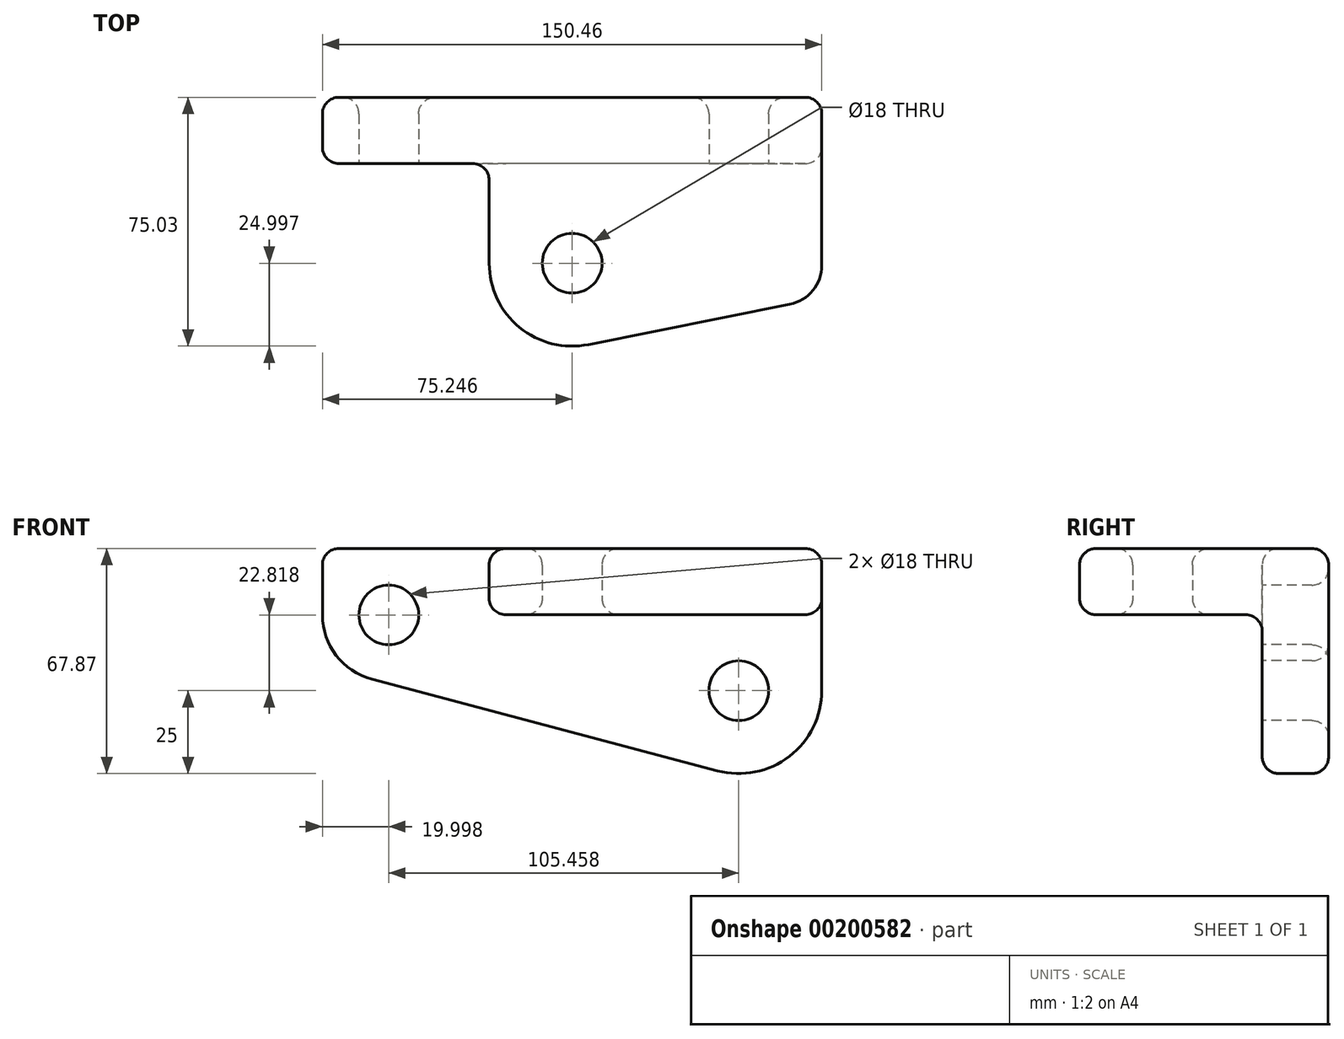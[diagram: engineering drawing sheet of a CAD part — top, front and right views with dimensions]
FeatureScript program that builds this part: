
annotation { "Feature Type Name" : "Feature", "Feature Type Description" : "" }
export const myFeature = defineFeature(function(context is Context, id is Id, definition is map)
    precondition{}
    {
        {
            var Q0;
            Q0=qCreatedBy(makeId("Front.planeOp"),FACE);
            var sketch = newSketch(context, id + "F0", { "sketchPlane" : qUnion([Q0])});
            skLineSegment(sketch, "E0", {"start": v(-25.6, -12.8) * mm, "end": v(-25.6, 22.64) * mm});
            skLineSegment(sketch, "E1", {"start": v(-25.6, 22.64) * mm, "end": v(124.87, 22.64) * mm});
            skLineSegment(sketch, "E2", {"start": v(124.87, 22.64) * mm, "end": v(124.87, -52.73) * mm});
            skLineSegment(sketch, "E3", {"start": v(124.87, -52.73) * mm, "end": v(-25.6, -12.8) * mm});
            skSolve(sketch);
        }
        {
            var Q0;
            Q0 = qSketchRegion(id + "F0", true);
            extrude(context, id + "F1", {"entities" : qUnion([Q0]), "depth" : 20 * mm});
        }
        {
            var Q0;
            Q0=makeQuery(id+"F1.opExtrude","SWEPT_FACE",FACE,{"disambiguationData":[OSD([sQuery(id+"F0.wireOp",EDGE,"E1")])]});
            var sketch = newSketch(context, id + "F2", { "sketchPlane" : qUnion([Q0])});
            skLineSegment(sketch, "E4", {"start": v(124.87, 0) * mm, "end": v(124.87, -60.48) * mm});
            skLineSegment(sketch, "E5", {"start": v(124.87, 0) * mm, "end": v(24.66, 0) * mm});
            skLineSegment(sketch, "E6", {"start": v(24.66, 0) * mm, "end": v(24.66, -80.53) * mm});
            skLineSegment(sketch, "E7", {"start": v(24.66, -80.53) * mm, "end": v(124.87, -60.48) * mm});
            skSolve(sketch);
        }
        {
            var Q0;
            Q0 = qSketchRegion(id + "F2", true);
            extrude(context, id + "F3", {"entities" : qUnion([Q0]), "operationType" : NewBodyOperationType.ADD, "oppositeDirection" : true, "depth" : 20 * mm});
        }
        {
            var Q0;
            Q0=makeQuery(id+"F3.opExtrude","SWEPT_EDGE",EDGE,{"disambiguationData":[OSD([sQuery(id+"F2.wireOp",EDGE,"E6"),sQuery(id+"F2.wireOp",EDGE,"E7")])]});
            var Q1;
            Q1=makeQuery(id+"F1.opExtrude","SWEPT_EDGE",EDGE,{"disambiguationData":[OSD([sQuery(id+"F0.wireOp",EDGE,"E2"),sQuery(id+"F0.wireOp",EDGE,"E3")])]});
            fillet(context, id + "F4", {"entities" : qUnion([Q0, Q1]), "radius" : 25 * mm, "tangentPropagation" : true, "allowEdgeOverflow" : false});
        }
        {
            var Q0;
            Q0=makeQuery(id+"F1.opExtrude","SWEPT_EDGE",EDGE,{"disambiguationData":[OSD([sQuery(id+"F0.wireOp",EDGE,"E0"),sQuery(id+"F0.wireOp",EDGE,"E3")])]});
            fillet(context, id + "F5", {"entities" : qUnion([Q0]), "radius" : 20 * mm, "tangentPropagation" : true, "allowEdgeOverflow" : false});
        }
        {
            var Q0;
            Q0=makeQuery(id+"F3.opExtrude","SWEPT_EDGE",EDGE,{"disambiguationData":[OSD([sQuery(id+"F2.wireOp",EDGE,"E4"),sQuery(id+"F2.wireOp",EDGE,"E7")])]});
            fillet(context, id + "F6", {"entities" : qUnion([Q0]), "radius" : 12 * mm, "tangentPropagation" : true, "allowEdgeOverflow" : false});
        }
        {
            var Q0;
            Q0=makeQuery(id+"F1.opExtrude","CAP_FACE",FACE,{"disambiguationData":[OSD([sQuery(id+"F0.wireOp",EDGE,"E0"),sQuery(id+"F0.wireOp",EDGE,"E1"),sQuery(id+"F0.wireOp",EDGE,"E2"),sQuery(id+"F0.wireOp",EDGE,"E3")])],"isStart":false});
            var sketch = newSketch(context, id + "F7", { "sketchPlane" : qUnion([Q0])});
            skPoint(sketch, "E8", {"position": v(99.87, -20.23) * mm});
            skPoint(sketch, "E9", {"position": v(-5.6, 2.59) * mm});
            skSolve(sketch);
        }
        {
            var Q0;
            Q0=makeQuery(id+"F3.opExtrude","CAP_FACE",FACE,{"disambiguationData":[OSD([sQuery(id+"F2.wireOp",EDGE,"E4"),sQuery(id+"F2.wireOp",EDGE,"E5"),sQuery(id+"F2.wireOp",EDGE,"E6"),sQuery(id+"F2.wireOp",EDGE,"E7")])],"isStart":false});
            var sketch = newSketch(context, id + "F8", { "sketchPlane" : qUnion([Q0])});
            skPoint(sketch, "E10", {"position": v(49.66, 50.03) * mm});
            skSolve(sketch);
        }
        {
            var Q0;
            Q0=sQuery(id+"F7.wireOp",VERTEX,"E9");
            var Q1;
            Q1=sQuery(id+"F7.wireOp",VERTEX,"E8");
            var Q2;
            Q2=sQuery(id+"F8.wireOp",VERTEX,"E10");
            var Q3;
            Q3=makeQuery(id+"F1.opExtrude","SWEPT_BODY",BODY,{"disambiguationData":[OSD([sQuery(id+"F0.wireOp",EDGE,"E0"),sQuery(id+"F0.wireOp",EDGE,"E1"),sQuery(id+"F0.wireOp",EDGE,"E2"),sQuery(id+"F0.wireOp",EDGE,"E3")])]});
            hole(context, id + "F9", {"style" : HoleStyle.SIMPLE, "endStyle" : HoleEndStyle.THROUGH, "holeDiameter" : 18 * mm, "locations" : qUnion([Q0, Q1, Q2]), "scope" : qUnion([Q3]), "isTappedThrough" : true});
        }
        {
            var Q0;
            Q0=makeQuery(id+"F1.opExtrude","CAP_FACE",FACE,{"disambiguationData":[OSD([sQuery(id+"F0.wireOp",EDGE,"E0"),sQuery(id+"F0.wireOp",EDGE,"E1"),sQuery(id+"F0.wireOp",EDGE,"E2"),sQuery(id+"F0.wireOp",EDGE,"E3")])],"isStart":true});
            var Q1;
            Q1=makeQuery(id+"F3.boolean.opBoolean","MERGE",FACE,{"derivedFrom":[makeQuery(id+"F1.opExtrude","SWEPT_FACE",FACE,{"disambiguationData":[OSD([sQuery(id+"F0.wireOp",EDGE,"E1")])]}),makeQuery(id+"F3.opExtrude","CAP_FACE",FACE,{"disambiguationData":[OSD([sQuery(id+"F2.wireOp",EDGE,"E4"),sQuery(id+"F2.wireOp",EDGE,"E5"),sQuery(id+"F2.wireOp",EDGE,"E6"),sQuery(id+"F2.wireOp",EDGE,"E7")])],"isStart":true})]});
            var Q2;
            Q2=makeQuery(id+"F3.boolean.opBoolean","MERGE",FACE,{"derivedFrom":[makeQuery(id+"F1.opExtrude","SWEPT_FACE",FACE,{"disambiguationData":[OSD([sQuery(id+"F0.wireOp",EDGE,"E2")])]}),makeQuery(id+"F3.opExtrude","SWEPT_FACE",FACE,{"disambiguationData":[OSD([sQuery(id+"F2.wireOp",EDGE,"E4")])]})]});
            var Q3;
            Q3=makeQuery(id+"F3.opExtrude","SWEPT_FACE",FACE,{"disambiguationData":[OSD([sQuery(id+"F2.wireOp",EDGE,"E7")])]});
            var Q4;
            Q4=makeQuery(id+"F1.opExtrude","SWEPT_FACE",FACE,{"disambiguationData":[OSD([sQuery(id+"F0.wireOp",EDGE,"E0")])]});
            var Q5;
            Q5=makeQuery(id+"F5.opFillet","BLEND_FACE",FACE,{"disambiguationData":[OSD([sQuery(id+"F0.wireOp",EDGE,"E0"),sQuery(id+"F0.wireOp",EDGE,"E3")])]});
            var Q6;
            Q6=makeQuery(id+"F9.hole-1.boolean.opBoolean","COPY",FACE,{"derivedFrom":makeQuery(id+"F9.hole-1.opRevolve","SWEPT_FACE",FACE,{"disambiguationData":[OSD([sQuery(id+"F9.hole-1.sketch.wireOp",EDGE,"core_line_2")])]})});
            var Q7;
            Q7=makeQuery(id+"F9.hole-0.boolean.opBoolean","COPY",FACE,{"derivedFrom":makeQuery(id+"F9.hole-0.opRevolve","SWEPT_FACE",FACE,{"disambiguationData":[OSD([sQuery(id+"F9.hole-0.sketch.wireOp",EDGE,"core_line_2")])]})});
            var Q8;
            Q8=makeQuery(id+"F1.opExtrude","SWEPT_FACE",FACE,{"disambiguationData":[OSD([sQuery(id+"F0.wireOp",EDGE,"E3")])]});
            var Q9;
            Q9=makeQuery(id+"F4.opFillet","BLEND_FACE",FACE,{"disambiguationData":[OSD([sQuery(id+"F0.wireOp",EDGE,"E2"),sQuery(id+"F0.wireOp",EDGE,"E3")])]});
            var Q10;
            Q10=makeQuery(id+"F4.opFillet","BLEND_FACE",FACE,{"disambiguationData":[OSD([sQuery(id+"F2.wireOp",EDGE,"E6"),sQuery(id+"F2.wireOp",EDGE,"E7")])]});
            var Q11;
            Q11=makeQuery(id+"F3.opExtrude","SWEPT_FACE",FACE,{"disambiguationData":[OSD([sQuery(id+"F2.wireOp",EDGE,"E6")])]});
            var Q12;
            Q12=makeQuery(id+"F3.opExtrude","CAP_FACE",FACE,{"disambiguationData":[OSD([sQuery(id+"F2.wireOp",EDGE,"E4"),sQuery(id+"F2.wireOp",EDGE,"E5"),sQuery(id+"F2.wireOp",EDGE,"E6"),sQuery(id+"F2.wireOp",EDGE,"E7")])],"isStart":false});
            fillet(context, id + "F10", {"entities" : qUnion([Q0, Q1, Q2, Q3, Q4, Q5, Q6, Q7, Q8, Q9, Q10, Q11, Q12]), "radius" : 5 * mm, "tangentPropagation" : true, "allowEdgeOverflow" : false});
        }
    });
